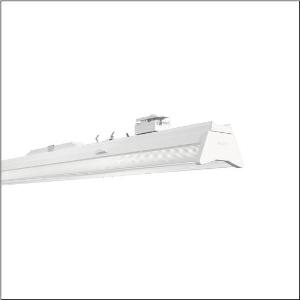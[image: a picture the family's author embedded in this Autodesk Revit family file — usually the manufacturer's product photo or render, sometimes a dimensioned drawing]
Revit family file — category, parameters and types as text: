
# Revit family: licross_r__11_performance_mo_51tm16dn445g_758e
name_source: partatom
category: Lighting Fixtures
units: mm (PartAtom-declared; Revit-internal decimal feet)

## family parameters
Cut with Voids When Loaded = No
Host = Face
Light Source = No
Part Type = Normal
Room Calculation Point = No
Round Connector Dimension = Use Diameter
Shared = No

## types (1)
- --- (1 x LED, 4520 lm, 24.3 W, 4000K)
    Apparent Load = 24 VA
    CIE Flux Codes = 66 88 96 79 100
    Color Rendering = 80
    Color Temperature = 4000K
    Default Elevation = 1800 mm
    Description = Licross® 11 Performance MO, luminaire insert, of sheet steel, galvanised, coil coated, white, length: 1.500mm, width: 120mm, height: 123mm, LED rated luminous flux: 4.520lm, light colour: 840, control gear: DALI 2, with plug, 5-pole, with phase selection, mains connection: 220..240V, AC, 50/60Hz, rated input power: 24W, halogen-free wiring, primary light control with lens, of plastic, primary optical cover: cover, of PMMA, CAT 2 (L<= 3000cd/m²), light emission: direct/indirect distribution, primary light characteristic: symmetric, protection rating (complete): IP40, insulation class (complete): insulation class I (protective earthing), certification: CE, ENEC, VDE, UKCA, protection symbol: D if used in an environment without relevant dust loads with corresponding accessories, impact resistance: IK06, permissible ambient temperature for indoor applications: -25..+45°C, corresponds to IFS (International Featured Standards) requirements for safety and quality in the food industry, reducing of maximum allowable ambient temperature of 5°C with ceiling mounting, LABS conformity tested according to VDMA 24364:2018-05, packaging unit: 1 piece
    Height = 114 mm
    Lamp = 1 x LED
    Lamp Light Flux = 4520 lm
    Lamp Power = 24.3 W
    Lamp count = 1
    Length = 1500 mm
    Luminous efficacy = 186 lm/W
    Manufacturer = Siteco
    ModVariant = No
    Model = 51TM16DN445G
    Mounting Place = Ceiling
    Mounting Type = Pendant
    Number of Poles = 1
    OnlyDefault = Yes
    Power Factor = 1
    Product Name = Licross® 11 Performance MO
    Product group = luminaire insert
    ProductGroupID = 901
    Protection Class = Protection class I
    Protection Degree = IP 40
    RLX_Detail_Level = 1
    RLX_Emergency_Light_Flux = 0 lm
    RLX_Emergency_Type = 0
    RLX_Emergency_Type_DB = No
    RlxData = <blob elided: 33801 chars, md5=234225db>
    Socket = socket
    Standby Power = 0 W
    System Light Flux = 4520 lm
    System Power = 24 W
    Type Comments = factory setting: luminous flux: 100 % | dim-lin: 254 | 161 mA
    Type Image = l_1256138.jpg
    URL = http://relux.com
    VarID = @adj_015981
    Voltage = 0 V
    Weight = 0.00 kg
    Width = 120 mm

## geometry (parser evidence)
native form markers: Blend x4, Sweep x13
no freeform markers — native parametric forms only
